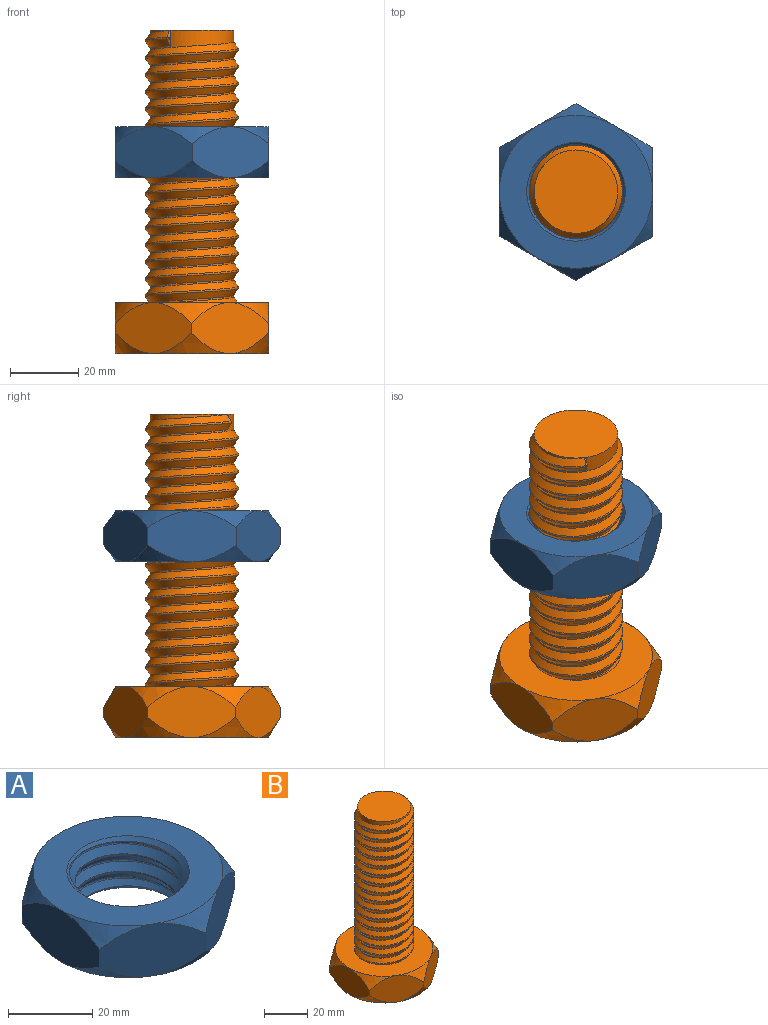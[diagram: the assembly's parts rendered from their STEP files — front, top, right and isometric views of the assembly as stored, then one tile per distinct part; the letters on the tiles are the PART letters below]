
ASSEMBLY  parts=2 mates=1
PART A: 26 faces, bbox 55x55x21.7 mm
  f0: plane 45x45mm, normal (0,0,1), area 929.9mm2, adj f5,f6,f8,f10,f12,f14,f22
  f1: plane 45x45mm, normal (0,0,-1), area 929.9mm2, adj f3,f4,f7,f9,f11,f13,f21
  f2: cylinder r=12.5mm len=25mm, axis (0,0,-1), area 86.5mm2, adj f21,f22,f23,f24
  f3: cone r=27.75mm half-angle=35deg, axis (0,0,1), area 75.2mm2, adj f1,f15,f16
  f4: cone r=27.75mm half-angle=35deg, axis (0,0,1), area 75.2mm2, adj f1,f15,f20
  f5: cone r=27.75mm half-angle=35deg, axis (0,0,-1), area 75.2mm2, adj f0,f15,f16
  f6: cone r=27.75mm half-angle=35deg, axis (0,0,-1), area 75.2mm2, adj f0,f15,f20
  f7: cone r=27.75mm half-angle=35deg, axis (0,0,1), area 75.2mm2, adj f1,f16,f17
  f8: cone r=27.75mm half-angle=35deg, axis (0,0,-1), area 75.2mm2, adj f0,f16,f17
  f9: cone r=27.75mm half-angle=35deg, axis (0,0,1), area 75.2mm2, adj f1,f17,f18
  f10: cone r=27.75mm half-angle=35deg, axis (0,0,-1), area 75.2mm2, adj f0,f17,f18
  f11: cone r=27.75mm half-angle=35deg, axis (0,0,1), area 75.2mm2, adj f1,f18,f19
  f12: cone r=27.75mm half-angle=35deg, axis (0,0,-1), area 75.2mm2, adj f0,f18,f19
  f13: cone r=27.75mm half-angle=35deg, axis (0,0,1), area 75.2mm2, adj f1,f19,f20
  f14: cone r=27.75mm half-angle=35deg, axis (0,0,-1), area 75.2mm2, adj f0,f19,f20
  f15: plane 25.5x18mm, normal (-0.5,-0.87,0), area 301.1mm2, adj f3,f4,f5,f6,f16,f20
  f16: plane 29x18mm, normal (-1,0,0), area 301.1mm2, adj f3,f5,f7,f8,f15,f17
  f17: plane 25.5x18mm, normal (-0.5,0.87,0), area 301.1mm2, adj f7,f8,f9,f10,f16,f18
  f18: plane 25.5x18mm, normal (0.5,0.87,0), area 301.1mm2, adj f9,f10,f11,f12,f17,f19
  f19: plane 29x18mm, normal (1,0,0), area 301.1mm2, adj f11,f12,f13,f14,f18,f20
  f20: plane 25.5x18mm, normal (0.5,-0.87,0), area 301.1mm2, adj f4,f6,f13,f14,f15,f19
  f21: cone r=14.5mm half-angle=45deg, axis (0,0,-1), area 159.4mm2, adj f1,f2,f23,f24,f25
  f22: cone r=12.5mm half-angle=45deg, axis (0,0,1), area 159.1mm2, adj f0,f2,f23,f24,f25
  f23: bspline ~32.51x28.15mm, area 492mm2, adj f2,f21,f22,f25
  f24: bspline ~32.51x28.15mm, area 493.1mm2, adj f2,f21,f22,f25
  f25: bspline ~28.16x28.16mm, area 147.5mm2, adj f21,f22,f23,f24
PART B: 46 faces, bbox 55.3x55.3x98.6 mm
  f0: plane 45.94x45.94mm, normal (0,0,1), area 1062.5mm2, adj f1,f15,f16,f17,f18,f19,f20,f43
  f1: cone r=22.5mm half-angle=30deg, axis (0,0,-1), area 86.2mm2, adj f0,f2,f14
  f2: plane 25.83x18.35mm, normal (0.5,-0.87,0), area 282.3mm2, adj f1,f3,f12,f13,f14,f19
  f3: cone r=22.5mm half-angle=30deg, axis (0,0,1), area 86.2mm2, adj f2,f4,f13
  f4: plane 45x45mm, normal (0,0,-1), area 1590.4mm2, adj f3,f5,f9,f10,f11,f12
  f5: cone r=22.5mm half-angle=30deg, axis (0,0,1), area 86.2mm2, adj f4,f6,f8
  f6: plane 25.83x18.35mm, normal (-0.5,0.87,0), area 282.3mm2, adj f5,f7,f8,f9,f16,f17
  f7: plane 29.33x18.35mm, normal (-1,0,0), area 282.3mm2, adj f6,f9,f10,f14,f15,f16
  f8: plane 25.83x18.35mm, normal (0.5,0.87,0), area 282.3mm2, adj f5,f6,f11,f13,f17,f18
  f9: cone r=22.5mm half-angle=30deg, axis (0,0,1), area 86.2mm2, adj f4,f6,f7
  f10: cone r=22.5mm half-angle=30deg, axis (0,0,1), area 86.2mm2, adj f4,f7,f14
  f11: cone r=22.5mm half-angle=30deg, axis (0,0,1), area 86.2mm2, adj f4,f8,f13
  f12: cone r=22.5mm half-angle=30deg, axis (0,0,1), area 86.2mm2, adj f2,f4,f14
  f13: plane 29.33x18.35mm, normal (1,0,0), area 282.3mm2, adj f2,f3,f8,f11,f18,f19
  f14: plane 25.83x18.35mm, normal (-0.5,-0.87,0), area 282.3mm2, adj f1,f2,f7,f10,f12,f15
  f15: cone r=22.5mm half-angle=30deg, axis (0,0,-1), area 86.2mm2, adj f0,f7,f14
  f16: cone r=22.5mm half-angle=30deg, axis (0,0,-1), area 86.2mm2, adj f0,f6,f7
  f17: cone r=22.5mm half-angle=30deg, axis (0,0,-1), area 86.2mm2, adj f0,f6,f8
  f18: cone r=22.5mm half-angle=30deg, axis (0,0,-1), area 86.2mm2, adj f0,f8,f13
  f19: cone r=22.5mm half-angle=30deg, axis (0,0,-1), area 86.2mm2, adj f0,f2,f13
  f20: bspline ~78.68x27.66mm, area 818.5mm2, adj f0,f21,f43,f45
  f21: sphere r=0.5mm, area 0.1mm2, adj f20,f22,f42
  f22: bspline ~3.04x2.34mm, area 1.6mm2, adj f21,f23,f26,f41,f43
  f23: plane 2.73x0.96mm, normal (0,1,0), area 1.3mm2, adj f22,f24,f42
  f24: cylinder r=12.25mm len=24.5mm, axis (0,0,-1), area 192.6mm2, adj f23,f25,f26,f42,f45
  f25: plane 24.5x24.5mm, normal (0,0,1), area 471.4mm2, adj f24
  f26: cylinder r=12.25mm len=24.5mm, axis (0,0,-1), area 39mm2, adj f22,f24,f27,f43,f45
  f27: cylinder r=12.25mm len=24.5mm, axis (0,0,-1), area 38.5mm2, adj f26,f28,f43,f45
  f28: cylinder r=12.25mm len=24.5mm, axis (0,0,-1), area 38.5mm2, adj f27,f29,f43,f45
  f29: cylinder r=12.25mm len=24.5mm, axis (0,0,-1), area 38.7mm2, adj f28,f30,f43,f45
  f30: cylinder r=12.25mm len=24.5mm, axis (0,0,-1), area 38.6mm2, adj f29,f31,f43,f45
  f31: cylinder r=12.25mm len=24.5mm, axis (0,0,-1), area 38.4mm2, adj f30,f32,f43,f45
  f32: cylinder r=12.25mm len=24.5mm, axis (0,0,-1), area 38.4mm2, adj f31,f33,f43,f45
  f33: cylinder r=12.25mm len=24.5mm, axis (0,0,-1), area 38.6mm2, adj f32,f34,f43,f45
  f34: cylinder r=12.25mm len=24.5mm, axis (0,0,-1), area 38.5mm2, adj f33,f35,f43,f45
  f35: cylinder r=12.25mm len=24.5mm, axis (0,0,-1), area 38.3mm2, adj f34,f36,f43,f45
  f36: cylinder r=12.25mm len=24.5mm, axis (0,0,-1), area 38.4mm2, adj f35,f37,f43,f45
  f37: cylinder r=12.25mm len=24.5mm, axis (0,0,-1), area 38.5mm2, adj f36,f38,f43,f45
  f38: cylinder r=12.25mm len=24.5mm, axis (0,0,-1), area 38.4mm2, adj f37,f39,f43,f45
  f39: cylinder r=12.25mm len=24.5mm, axis (0,0,-1), area 38.3mm2, adj f38,f40,f43,f45
  f40: cylinder r=12.25mm len=24.5mm, axis (0,0,-1), area 38.4mm2, adj f39,f43,f44,f45
  f41: sphere r=0.5mm, area 0mm2, adj f22,f42
  f42: bspline ~2.96x2.3mm, area 1.7mm2, adj f21,f23,f24,f41,f45
  f43: bspline ~79.75x31.93mm, area 2979.9mm2, adj f0,f20,f22,f26,f27,f28,f29,f30
  f44: cylinder r=12.25mm len=7.16mm, axis (0,0,-1), area 1.9mm2, adj f0,f40,f43
  f45: bspline ~82.25x31.93mm, area 3069.5mm2, adj f0,f20,f24,f26,f27,f28,f29,f30
PLACE A t=(6.64,0.07,14.05)mm fixed
PLACE B rot(axis=(0,0,-1),120.5deg) t=(6.64,0.07,-22.63)mm
MATE cylindrical B.f1 <-> A.f3  axis (0,0,-1) through (6.64,0.07,-37.63)mm
